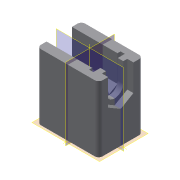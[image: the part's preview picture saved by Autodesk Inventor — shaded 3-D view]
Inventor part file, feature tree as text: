
AUTODESK INVENTOR PART (.ipt)
format: ipt  version: 2015 SP2 (Build 190223200, 223)  size: 174,592 bytes
history: native  units: mm
features: extrude x7, sketch x7, other x1, fillet x1, plane x1, projected_geometry x1
ambient origin geometry x8: Origin, YZ Plane, XZ Plane, XY Plane, X Axis, Y Axis, Z Axis, Center Point
bodies: Body1 (feature_tree)
feature tree (18):
  other  "Sólido1"
  extrude  "Extrusión1"  Depth=23.0mm
  fillet  "Empalme1"  Radius=34.25mm
  extrude  "Extrusión2"  Depth=2.0mm
  extrude  "Extrusión3"  Depth=13.164mm
  extrude  "Extrusión4"  Depth=10.0mm
  extrude  "Extrusión5"  Depth=2.9mm TaperAngle=0.0deg
  extrude  "Extrusión6"  Depth=10.0mm
  extrude  "Extrusión7"  Depth=23.71mm TaperAngle=0.0deg
  plane  "Plano de trabajo1"
  sketch  "Boceto1"  dims[d0=32.0mm d1=23.0mm d2=34.25mm d3=0.0mm]
  sketch  "Boceto2"  dims[d4=2.0mm d5=13.8mm]
  sketch  "Boceto3"  dims[d6=7.6mm d7=13.164mm]
  projected_geometry  "Contorno proyectado1"
  sketch  "Boceto4"  dims[d8=3.19mm d9=0.0mm d10=10.0mm]
  sketch  "Boceto5"  dims[d11=8.993mm d12=2.9mm d13=0.0mm]
  sketch  "Boceto6"  dims[d14=23.71mm d15=0.0mm d16=10.0mm]
  sketch  "Boceto7"  dims[d17=16.4mm d18=23.71mm d19=0.0mm d20=3.78mm d21=3.78mm d22=10.0mm d23=11.0mm d24=7.21mm d25=0.0mm d26=3.747mm d27=3.747mm d28=7.21mm d29=0.0mm]
